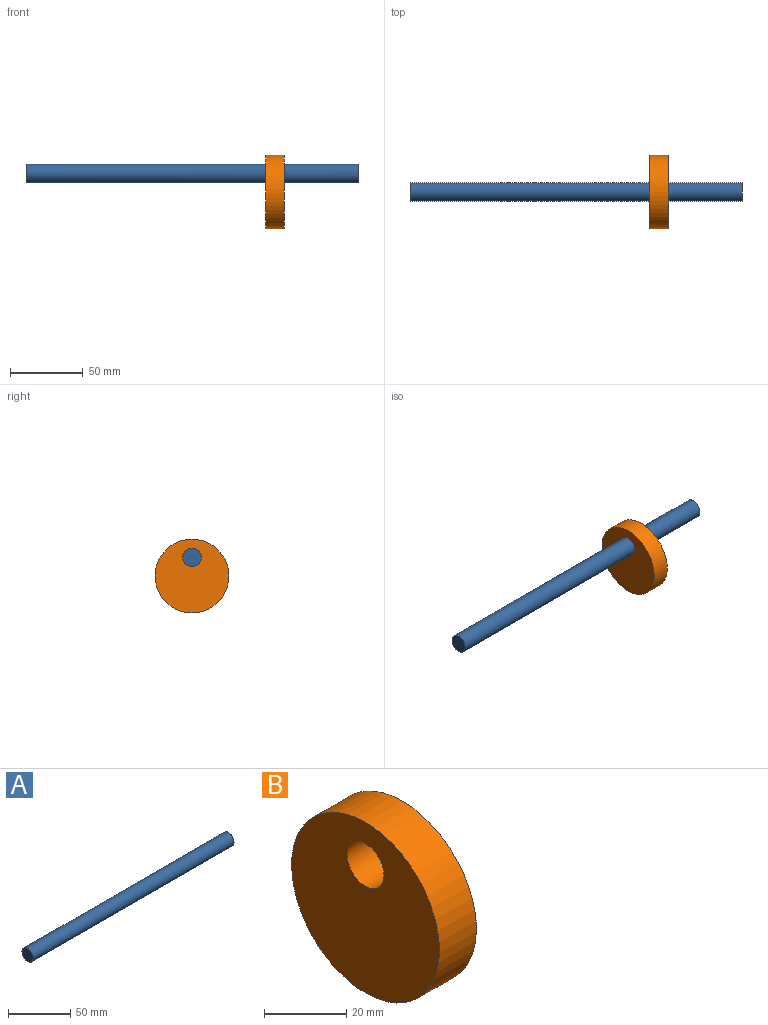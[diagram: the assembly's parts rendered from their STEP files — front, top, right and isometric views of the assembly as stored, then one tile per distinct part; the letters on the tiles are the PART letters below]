
ASSEMBLY  parts=2 mates=1
PART A: 3 faces, bbox 228.6x12.7x12.7 mm
  f0: plane 12.7x12.7mm, normal (-1,0,0), area 126.7mm2, adj f2
  f1: plane 12.7x12.7mm, normal (1,0,0), area 126.7mm2, adj f2
  f2: cylinder r=6.35mm len=228.6mm, axis (-1,0,0), area 9120.7mm2, adj f0,f1
PART B: 4 faces, bbox 12.7x50.8x50.8 mm
  f0: plane 50.8x50.8mm, normal (-1,0,0), area 1900.2mm2, adj f1,f3
  f1: cylinder r=25.4mm len=50.8mm, axis (-1,0,0), area 2026.8mm2, adj f0,f2
  f2: plane 50.8x50.8mm, normal (1,0,0), area 1900.2mm2, adj f1,f3
  f3: cylinder r=6.35mm len=12.7mm, axis (-1,0,0), area 506.7mm2, adj f0,f2
PLACE A t=(-228.6,0,-57.15)mm
PLACE B t=(-228.6,0,-57.15)mm
MATE fastened A.f2 <-> B.f3  axis (-1,0,0) through (-57.15,0,0)mm
